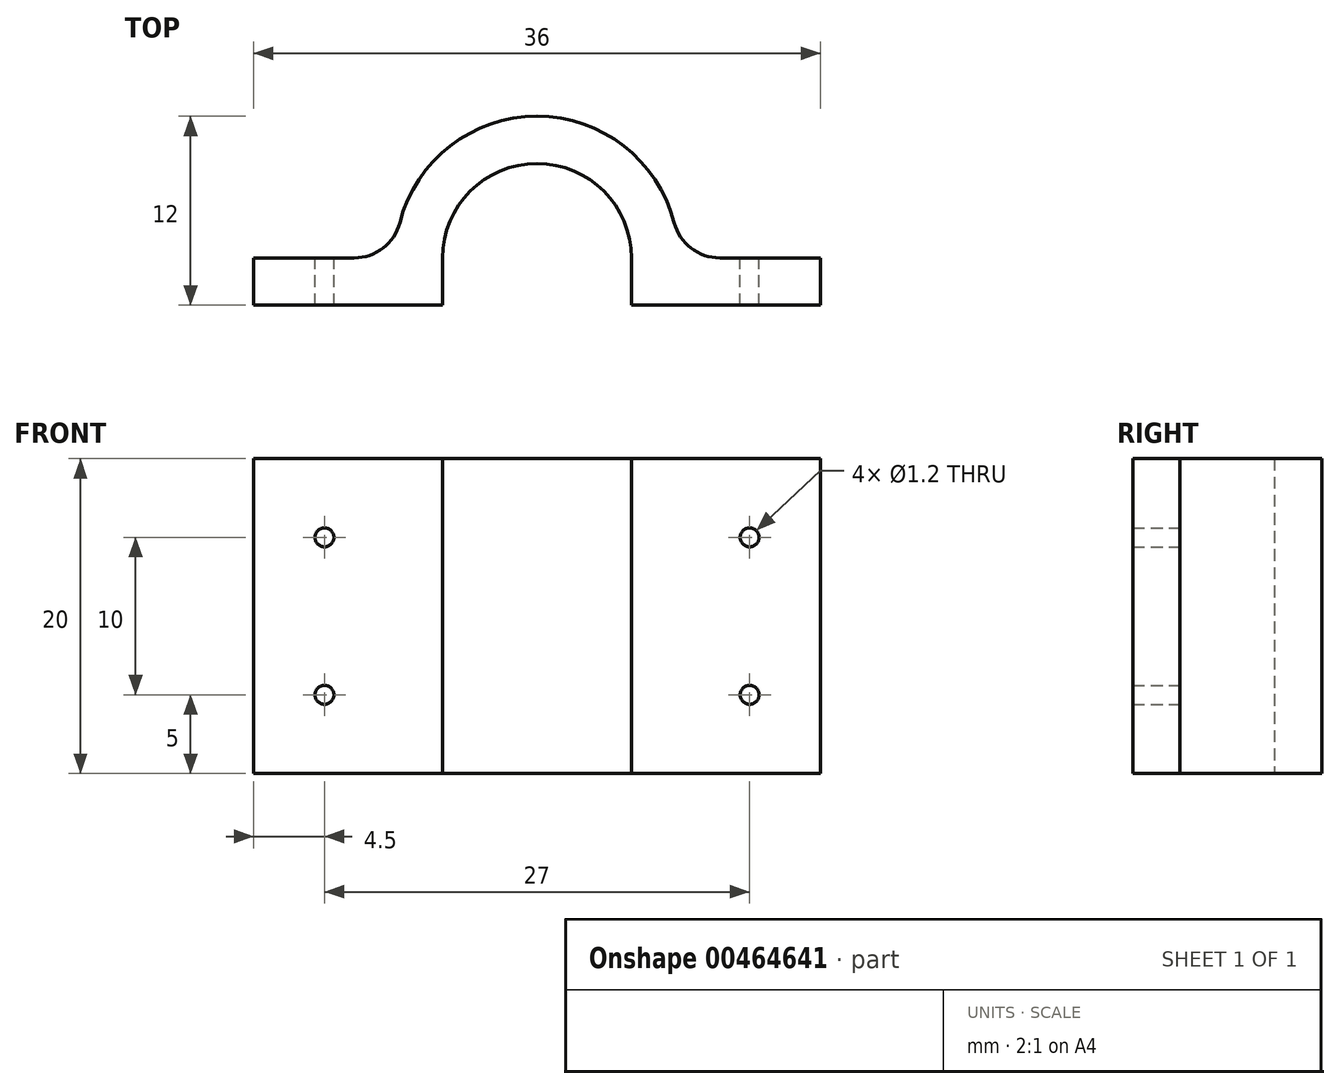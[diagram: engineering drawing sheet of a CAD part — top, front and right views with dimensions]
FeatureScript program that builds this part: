
annotation { "Feature Type Name" : "Feature", "Feature Type Description" : "" }
export const myFeature = defineFeature(function(context is Context, id is Id, definition is map)
    precondition{}
    {
        {
            var Q0;
            Q0=qCreatedBy(makeId("Top.planeOp"),FACE);
            var sketch = newSketch(context, id + "F0", { "sketchPlane" : qUnion([Q0])});
            skArc(sketch, "E0", {"start": v(6, 0) * mm, "mid": v(0, 6) * mm, "end": v(-6, 0) * mm});
            skArc(sketch, "E1.0", {"start": v(9, 0) * mm, "mid": v(0, 9) * mm, "end": v(-9, 0) * mm});
            skLineSegment(sketch, "E2.bottom", {"start": v(9, 0) * mm, "end": v(18, 0) * mm});
            skLineSegment(sketch, "E2.top", {"start": v(6, -3) * mm, "end": v(18, -3) * mm});
            skLineSegment(sketch, "E2.right", {"start": v(18, 0) * mm, "end": v(18, -3) * mm});
            skLineSegment(sketch, "E3.bottom", {"start": v(-9, 0) * mm, "end": v(-18, 0) * mm});
            skLineSegment(sketch, "E3.top", {"start": v(-6, -3) * mm, "end": v(-18, -3) * mm});
            skLineSegment(sketch, "E3.right", {"start": v(-18, 0) * mm, "end": v(-18, -3) * mm});
            skLineSegment(sketch, "E4", {"start": v(-6, 0) * mm, "end": v(-6, -3) * mm});
            skLineSegment(sketch, "E5", {"start": v(6, 0) * mm, "end": v(6, -3) * mm});
            skPoint(sketch, "E6.orphan", {"position": v(0, -3) * mm});
            skSolve(sketch);
        }
        {
            var Q0;
            Q0=makeQuery(id+"F0.imprint","IMPRINT",FACE,{"disambiguationData":[TD([[makeQuery(id+"F0.imprint","IMPRINT",EDGE,{"derivedFrom":sQuery(id+"F0.wireOp",EDGE,"E0")}),-1.0]])]});
            extrude(context, id + "F1", {"entities" : qUnion([Q0]), "depth" : 20 * mm});
        }
        {
            var Q0;
            Q0=makeQuery(id+"F1.opExtrude","SWEPT_FACE",FACE,{"disambiguationData":[OSD([sQuery(id+"F0.wireOp",EDGE,"E2.bottom")])]});
            var sketch = newSketch(context, id + "F2", { "sketchPlane" : qUnion([Q0])});
            skLineSegment(sketch, "E7", {"start": v(-17, 20) * mm, "end": v(-17, 0) * mm, "construction": true});
            skLineSegment(sketch, "E8", {"start": v(-9, 15) * mm, "end": v(-18, 15) * mm, "construction": true});
            skLineSegment(sketch, "E9", {"start": v(-9, 5) * mm, "end": v(-18, 5) * mm, "construction": true});
            skPoint(sketch, "E10", {"position": v(-13.5, 15) * mm});
            skPoint(sketch, "E11", {"position": v(-13.5, 5) * mm});
            skLineSegment(sketch, "E12", {"start": v(0, 0) * mm, "end": v(0, 20.25) * mm, "construction": true});
            skPoint(sketch, "E13.MirrorP", {"position": v(13.5, 5) * mm});
            skPoint(sketch, "E14.MirrorP", {"position": v(13.5, 15) * mm});
            skSolve(sketch);
        }
        {
            var Q0;
            Q0=sQuery(id+"F2.wireOp",VERTEX,"E10");
            var Q1;
            Q1=sQuery(id+"F2.wireOp",VERTEX,"E11");
            var Q2;
            Q2=sQuery(id+"F2.wireOp",VERTEX,"E14.MirrorP");
            var Q3;
            Q3=sQuery(id+"F2.wireOp",VERTEX,"E13.MirrorP");
            var Q4;
            Q4=makeQuery(id+"F1.opExtrude","SWEPT_BODY",BODY,{"disambiguationData":[OSD([sQuery(id+"F0.wireOp",EDGE,"E0"),sQuery(id+"F0.wireOp",EDGE,"E1.0"),sQuery(id+"F0.wireOp",EDGE,"E2.bottom"),sQuery(id+"F0.wireOp",EDGE,"E2.top"),sQuery(id+"F0.wireOp",EDGE,"E2.right"),sQuery(id+"F0.wireOp",EDGE,"E3.bottom"),sQuery(id+"F0.wireOp",EDGE,"E3.top"),sQuery(id+"F0.wireOp",EDGE,"E3.right"),sQuery(id+"F0.wireOp",EDGE,"E4"),sQuery(id+"F0.wireOp",EDGE,"E5")])]});
            hole(context, id + "F3", {"style" : HoleStyle.SIMPLE, "endStyle" : HoleEndStyle.THROUGH, "holeDiameter" : 1.2 * mm, "isTappedThrough" : true, "tappedDepth" : 12 * mm, "tapClearance" : 3, "startFromSketch" : true, "locations" : qUnion([Q0, Q1, Q2, Q3]), "scope" : qUnion([Q4])});
        }
        {
            var Q0;
            Q0=makeQuery(id+"F1.opExtrude","SWEPT_EDGE",EDGE,{"disambiguationData":[OSD([sQuery(id+"F0.wireOp",EDGE,"E1.0"),sQuery(id+"F0.wireOp",EDGE,"E2.bottom")])]});
            var Q1;
            Q1=makeQuery(id+"F1.opExtrude","SWEPT_EDGE",EDGE,{"disambiguationData":[OSD([sQuery(id+"F0.wireOp",EDGE,"E1.0"),sQuery(id+"F0.wireOp",EDGE,"E3.bottom")])]});
            fillet(context, id + "F4", {"entities" : qUnion([Q0, Q1]), "radius" : 3 * mm, "tangentPropagation" : true, "allowEdgeOverflow" : false});
        }
    });
